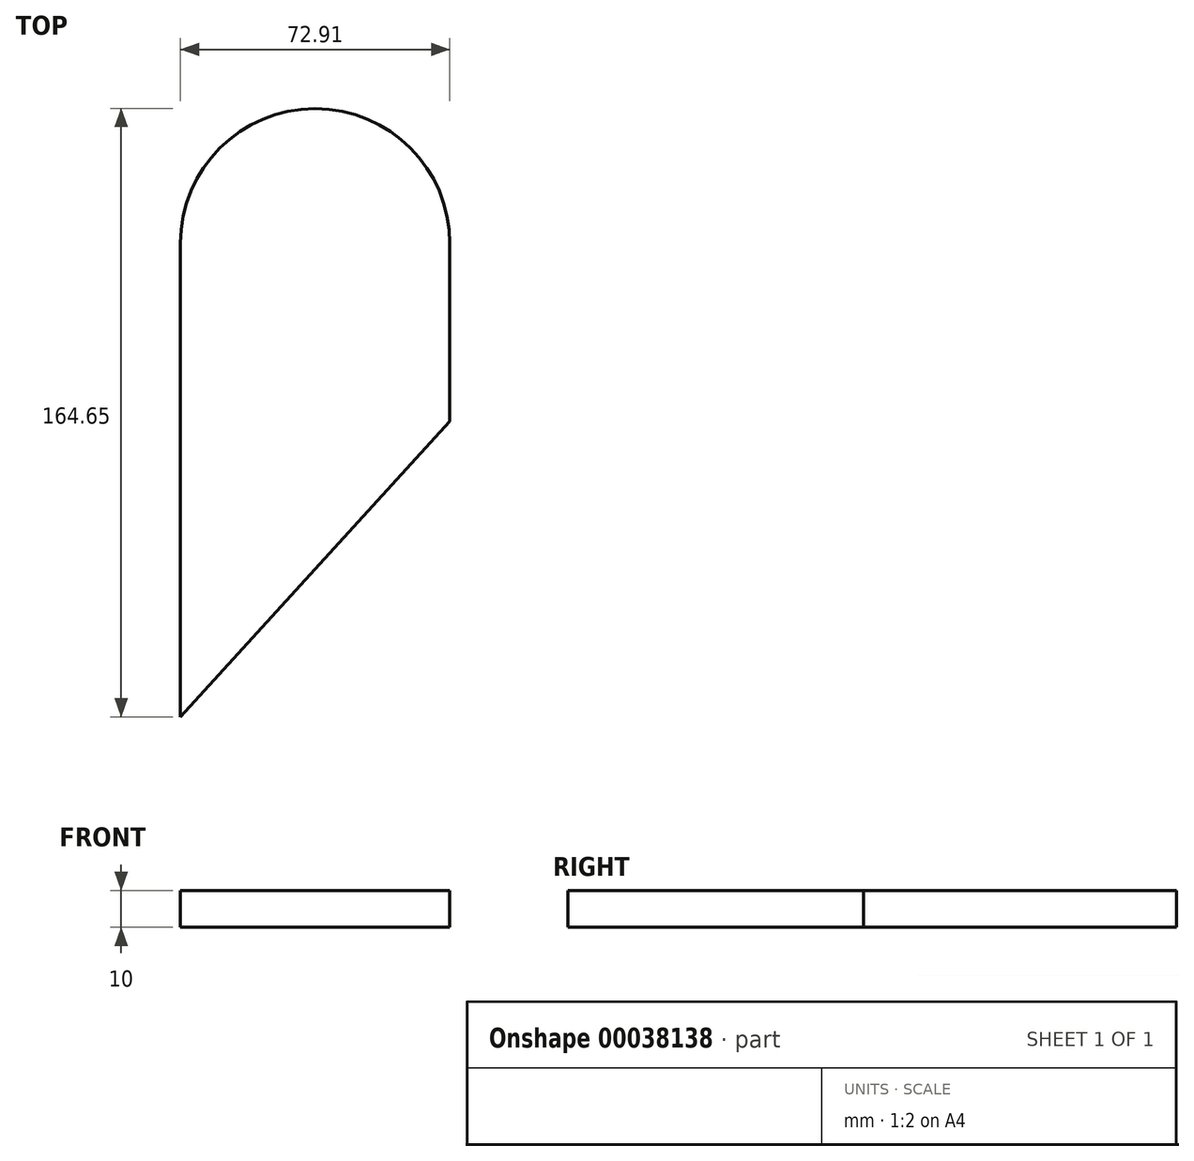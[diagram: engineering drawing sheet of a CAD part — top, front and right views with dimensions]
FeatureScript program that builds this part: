
annotation { "Feature Type Name" : "Feature", "Feature Type Description" : "" }
export const myFeature = defineFeature(function(context is Context, id is Id, definition is map)
    precondition{}
    {
        {
            var Q0;
            Q0=qCreatedBy(makeId("Top.planeOp"),FACE);
            var sketch = newSketch(context, id + "F0", { "sketchPlane" : qUnion([Q0])});
            skLineSegment(sketch, "E0.bottom", {"start": v(-52.22, 42.26) * mm, "end": v(20.69, 42.26) * mm});
            skLineSegment(sketch, "E0.top", {"start": v(-52.22, -5.94) * mm, "end": v(20.69, -5.94) * mm});
            skLineSegment(sketch, "E0.left", {"start": v(-52.22, 42.26) * mm, "end": v(-52.22, -5.94) * mm});
            skLineSegment(sketch, "E0.right", {"start": v(20.69, 42.26) * mm, "end": v(20.69, -5.94) * mm});
            skArc(sketch, "E1", {"start": v(20.69, 42.26) * mm, "mid": v(-15.77, 78.7) * mm, "end": v(-52.22, 42.26) * mm});
            skLineSegment(sketch, "E2", {"start": v(-52.22, -5.94) * mm, "end": v(-52.22, -85.94) * mm});
            skLineSegment(sketch, "E3", {"start": v(-52.22, -85.94) * mm, "end": v(20.69, -5.94) * mm});
            skSolve(sketch);
        }
        {
            var Q0;
            Q0=makeQuery(id+"F0.imprint","IMPRINT",FACE,{"disambiguationData":[TD([[makeQuery(id+"F0.imprint","IMPRINT",EDGE,{"derivedFrom":sQuery(id+"F0.wireOp",EDGE,"E0.bottom")}),1.0]])]});
            var Q1;
            Q1=makeQuery(id+"F0.imprint","IMPRINT",FACE,{"disambiguationData":[TD([[makeQuery(id+"F0.imprint","IMPRINT",EDGE,{"derivedFrom":sQuery(id+"F0.wireOp",EDGE,"E0.bottom")}),-1.0]])]});
            var Q2;
            Q2=makeQuery(id+"F0.imprint","IMPRINT",FACE,{"disambiguationData":[TD([[makeQuery(id+"F0.imprint","IMPRINT",EDGE,{"derivedFrom":sQuery(id+"F0.wireOp",EDGE,"E0.top")}),-1.0]])]});
            extrude(context, id + "F1", {"entities" : qUnion([Q0, Q1, Q2]), "depth" : 10 * mm});
        }
    });
